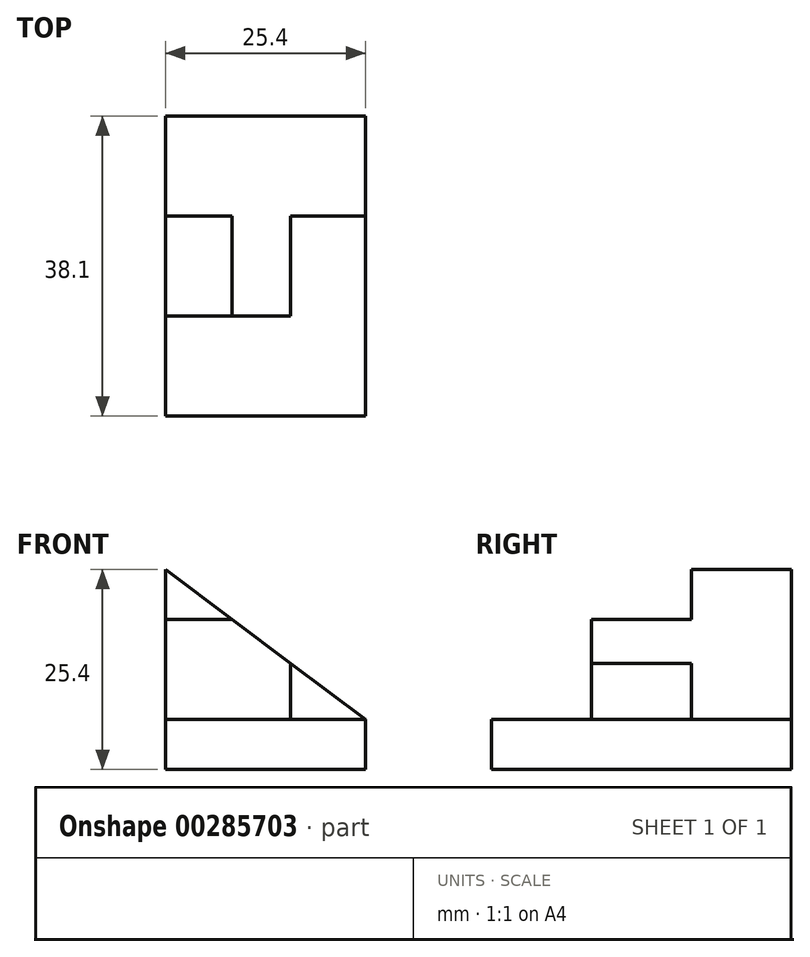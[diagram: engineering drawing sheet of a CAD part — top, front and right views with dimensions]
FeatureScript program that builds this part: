
annotation { "Feature Type Name" : "Feature", "Feature Type Description" : "" }
export const myFeature = defineFeature(function(context is Context, id is Id, definition is map)
    precondition{}
    {
        {
            var Q0;
            Q0=qCreatedBy(makeId("Front.planeOp"),FACE);
            var sketch = newSketch(context, id + "F0", { "sketchPlane" : qUnion([Q0])});
            skLineSegment(sketch, "E0.bottom", {"start": v(0, 0) * mm, "end": v(25.4, 0) * mm});
            skLineSegment(sketch, "E0.top", {"start": v(0, 6.35) * mm, "end": v(25.4, 6.35) * mm});
            skLineSegment(sketch, "E0.left", {"start": v(0, 0) * mm, "end": v(0, 6.35) * mm});
            skLineSegment(sketch, "E0.right", {"start": v(25.4, 0) * mm, "end": v(25.4, 6.35) * mm});
            skSolve(sketch);
        }
        {
            var Q0;
            Q0 = qSketchRegion(id + "F0", true);
            extrude(context, id + "F1", {"entities" : qUnion([Q0]), "oppositeDirection" : true, "depth" : 38.1 * mm});
        }
        {
            var Q0;
            Q0=makeQuery(id+"F1.opExtrude","SWEPT_FACE",FACE,{"disambiguationData":[OSD([sQuery(id+"F0.wireOp",EDGE,"E0.top")])]});
            var sketch = newSketch(context, id + "F2", { "sketchPlane" : qUnion([Q0])});
            skLineSegment(sketch, "E1.bottom", {"start": v(0, 38.1) * mm, "end": v(25.4, 38.1) * mm});
            skLineSegment(sketch, "E1.top", {"start": v(0, 25.4) * mm, "end": v(25.4, 25.4) * mm});
            skLineSegment(sketch, "E1.left", {"start": v(0, 38.1) * mm, "end": v(0, 25.4) * mm});
            skLineSegment(sketch, "E1.right", {"start": v(25.4, 38.1) * mm, "end": v(25.4, 25.4) * mm});
            skSolve(sketch);
        }
        {
            var Q0;
            Q0 = qSketchRegion(id + "F2", true);
            extrude(context, id + "F3", {"entities" : qUnion([Q0]), "operationType" : NewBodyOperationType.ADD, "depth" : 19.05 * mm});
        }
        {
            var Q0;
            Q0=makeQuery(id+"F3.opExtrude","SWEPT_FACE",FACE,{"disambiguationData":[OSD([sQuery(id+"F2.wireOp",EDGE,"E1.top")])]});
            var sketch = newSketch(context, id + "F4", { "sketchPlane" : qUnion([Q0])});
            skLineSegment(sketch, "E2", {"start": v(0, 25.4) * mm, "end": v(25.4, 6.35) * mm});
            skLineSegment(sketch, "E3", {"start": v(25.4, 6.35) * mm, "end": v(25.4, 25.4) * mm});
            skLineSegment(sketch, "E4", {"start": v(25.4, 25.4) * mm, "end": v(0, 25.4) * mm});
            skSolve(sketch);
        }
        {
            var Q0;
            Q0=makeQuery(id+"F4.imprint","IMPRINT",FACE,{"disambiguationData":[TD([[makeQuery(id+"F4.imprint","IMPRINT",EDGE,{"derivedFrom":sQuery(id+"F4.wireOp",EDGE,"E2")}),1.0]])]});
            extrude(context, id + "F5", {"entities" : qUnion([Q0]), "operationType" : NewBodyOperationType.REMOVE, "oppositeDirection" : true, "depth" : 12.7 * mm});
        }
        {
            var Q0;
            Q0=makeQuery(id+"F3.opExtrude","SWEPT_FACE",FACE,{"disambiguationData":[OSD([sQuery(id+"F2.wireOp",EDGE,"E1.top")])]});
            var sketch = newSketch(context, id + "F6", { "sketchPlane" : qUnion([Q0])});
            skLineSegment(sketch, "E5", {"start": v(0, 6.35) * mm, "end": v(0, 19.05) * mm});
            skLineSegment(sketch, "E6", {"start": v(0, 19.05) * mm, "end": v(8.47, 19.05) * mm});
            skLineSegment(sketch, "E7", {"start": v(0, 6.35) * mm, "end": v(15.88, 6.35) * mm});
            skLineSegment(sketch, "E8", {"start": v(15.88, 6.35) * mm, "end": v(15.88, 13.5) * mm});
            skLineSegment(sketch, "E9", {"start": v(15.88, 13.5) * mm, "end": v(8.47, 19.05) * mm});
            skSolve(sketch);
        }
        {
            var Q0;
            Q0=makeQuery(id+"F6.imprint","IMPRINT",FACE,{"disambiguationData":[TD([[makeQuery(id+"F6.imprint","IMPRINT",EDGE,{"derivedFrom":sQuery(id+"F6.wireOp",EDGE,"E5")}),1.0]])]});
            extrude(context, id + "F7", {"entities" : qUnion([Q0]), "operationType" : NewBodyOperationType.ADD, "depth" : 12.7 * mm});
        }
    });
